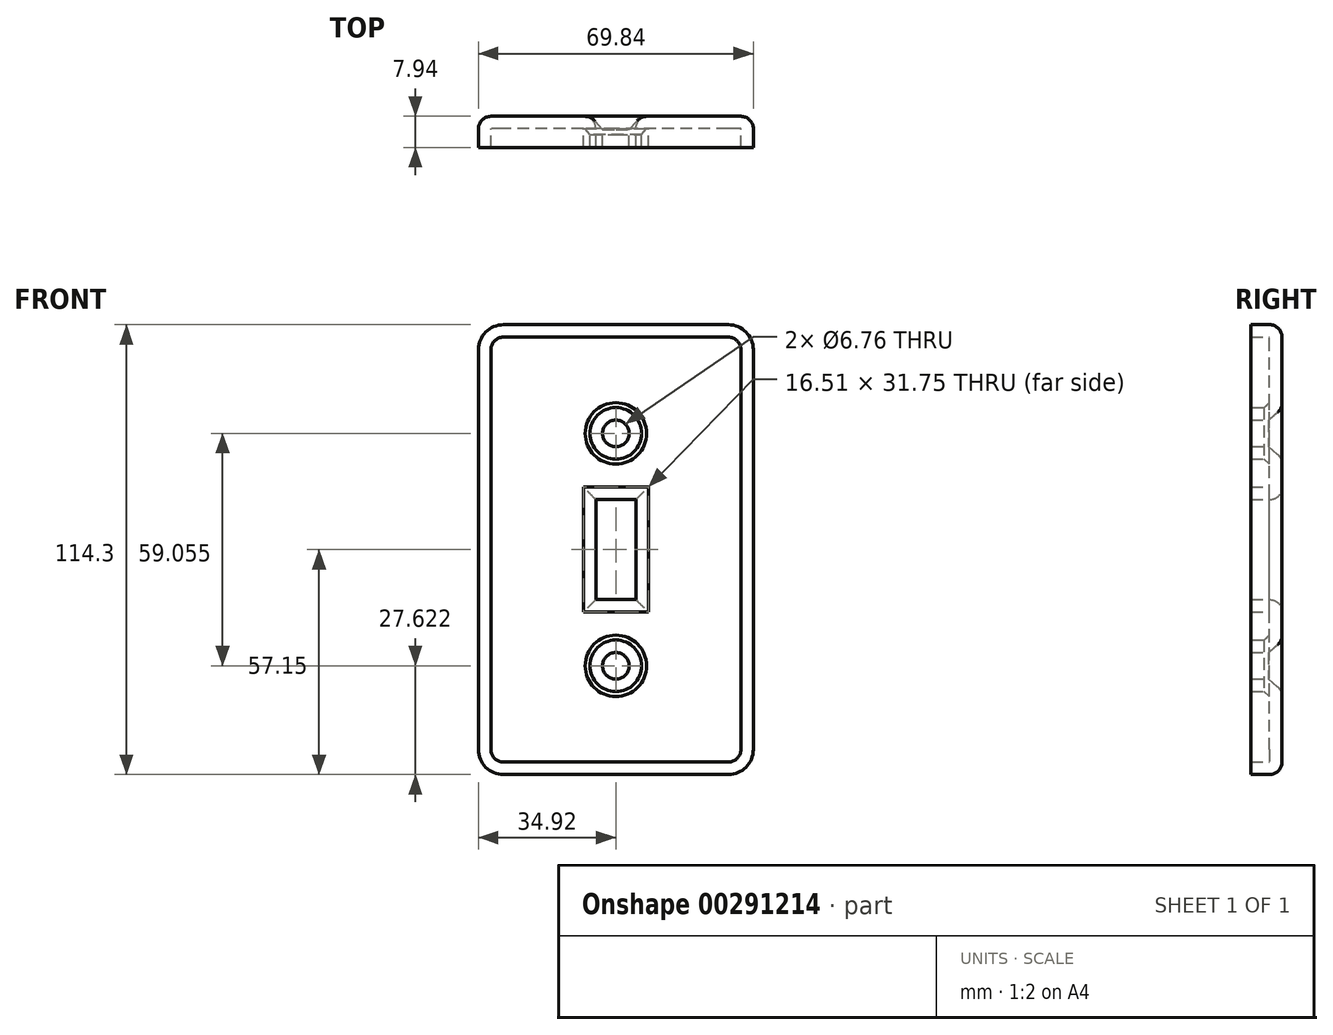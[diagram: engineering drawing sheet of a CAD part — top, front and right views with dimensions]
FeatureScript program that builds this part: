
annotation { "Feature Type Name" : "Feature", "Feature Type Description" : "" }
export const myFeature = defineFeature(function(context is Context, id is Id, definition is map)
    precondition{}
    {
        {
            var Q0;
            Q0=qCreatedBy(makeId("Front.planeOp"),FACE);
            var sketch = newSketch(context, id + "F0", { "sketchPlane" : qUnion([Q0])});
            skLineSegment(sketch, "E0.bottom", {"start": v(28.57, -57.15) * mm, "end": v(-28.57, -57.15) * mm});
            skLineSegment(sketch, "E0.top", {"start": v(28.58, 57.15) * mm, "end": v(-28.57, 57.15) * mm});
            skLineSegment(sketch, "E0.left", {"start": v(34.93, -50.8) * mm, "end": v(34.93, 50.8) * mm});
            skLineSegment(sketch, "E0.right", {"start": v(-34.92, -50.8) * mm, "end": v(-34.92, 50.8) * mm});
            skPoint(sketch, "E0.middle", {"position": v(0, 0) * mm});
            skPoint(sketch, "E1.visualSharp", {"position": v(-34.92, 57.15) * mm});
            skArc(sketch, "E1.filletArc", {"start": v(-28.57, 57.15) * mm, "mid": v(-33.07, 55.3) * mm, "end": v(-34.92, 50.8) * mm});
            skPoint(sketch, "E2.visualSharp", {"position": v(34.93, 57.15) * mm});
            skArc(sketch, "E2.filletArc", {"start": v(34.93, 50.8) * mm, "mid": v(33.07, 55.3) * mm, "end": v(28.58, 57.15) * mm});
            skPoint(sketch, "E3.visualSharp", {"position": v(34.92, -57.15) * mm});
            skArc(sketch, "E3.filletArc", {"start": v(28.57, -57.15) * mm, "mid": v(33.07, -55.3) * mm, "end": v(34.92, -50.8) * mm});
            skPoint(sketch, "E4.visualSharp", {"position": v(-34.93, -57.15) * mm});
            skArc(sketch, "E4.filletArc", {"start": v(-34.93, -50.8) * mm, "mid": v(-33.07, -55.3) * mm, "end": v(-28.57, -57.15) * mm});
            skLineSegment(sketch, "E5.bottom", {"start": v(5.08, -12.7) * mm, "end": v(-5.08, -12.7) * mm});
            skLineSegment(sketch, "E5.top", {"start": v(5.08, 12.7) * mm, "end": v(-5.08, 12.7) * mm});
            skLineSegment(sketch, "E5.left", {"start": v(5.08, -12.7) * mm, "end": v(5.08, 12.7) * mm});
            skLineSegment(sketch, "E5.right", {"start": v(-5.08, -12.7) * mm, "end": v(-5.08, 12.7) * mm});
            skPoint(sketch, "E6", {"position": v(0, 29.53) * mm});
            skPoint(sketch, "E7", {"position": v(0, -29.53) * mm});
            skSolve(sketch);
        }
        {
            var Q0;
            Q0=makeQuery(id+"F0.imprint","IMPRINT",FACE,{"disambiguationData":[TD([[makeQuery(id+"F0.imprint","IMPRINT",EDGE,{"derivedFrom":sQuery(id+"F0.wireOp",EDGE,"E0.bottom")}),-1.0]])]});
            extrude(context, id + "F1", {"entities" : qUnion([Q0]), "depth" : 7.94 * mm});
        }
        {
            var Q0;
            Q0=sQuery(id+"F0.wireOp",VERTEX,"E7");
            var Q1;
            Q1=sQuery(id+"F0.wireOp",VERTEX,"E6");
            var Q2;
            Q2=makeQuery(id+"F1.opExtrude","SWEPT_BODY",BODY,{"disambiguationData":[OSD([sQuery(id+"F0.wireOp",EDGE,"E0.bottom"),sQuery(id+"F0.wireOp",EDGE,"E0.top"),sQuery(id+"F0.wireOp",EDGE,"E0.left"),sQuery(id+"F0.wireOp",EDGE,"E0.right"),sQuery(id+"F0.wireOp",EDGE,"E1.filletArc"),sQuery(id+"F0.wireOp",EDGE,"E2.filletArc"),sQuery(id+"F0.wireOp",EDGE,"E3.filletArc"),sQuery(id+"F0.wireOp",EDGE,"E4.filletArc"),sQuery(id+"F0.wireOp",EDGE,"E5.bottom"),sQuery(id+"F0.wireOp",EDGE,"E5.top"),sQuery(id+"F0.wireOp",EDGE,"E5.left"),sQuery(id+"F0.wireOp",EDGE,"E5.right")])]});
            hole(context, id + "F2", {"style" : HoleStyle.C_SINK, "endStyle" : HoleEndStyle.THROUGH, "oppositeDirection" : true, "holeDiameter" : 6.76 * mm, "cSinkDiameter" : 12.7 * mm, "cSinkAngle" : 82 * degree, "tappedDepth" : 12.7 * mm, "tapClearance" : 3, "locations" : qUnion([Q0, Q1]), "scope" : qUnion([Q2])});
        }
        {
            var Q0;
            Q0=makeQuery(id+"F1.opExtrude","CAP_FACE",FACE,{"disambiguationData":[OSD([sQuery(id+"F0.wireOp",EDGE,"E0.bottom"),sQuery(id+"F0.wireOp",EDGE,"E0.top"),sQuery(id+"F0.wireOp",EDGE,"E0.left"),sQuery(id+"F0.wireOp",EDGE,"E0.right"),sQuery(id+"F0.wireOp",EDGE,"E1.filletArc"),sQuery(id+"F0.wireOp",EDGE,"E2.filletArc"),sQuery(id+"F0.wireOp",EDGE,"E3.filletArc"),sQuery(id+"F0.wireOp",EDGE,"E4.filletArc"),sQuery(id+"F0.wireOp",EDGE,"E5.bottom"),sQuery(id+"F0.wireOp",EDGE,"E5.top"),sQuery(id+"F0.wireOp",EDGE,"E5.left"),sQuery(id+"F0.wireOp",EDGE,"E5.right")])],"isStart":true});
            fillet(context, id + "F3", {"entities" : qUnion([Q0]), "radius" : 3.17 * mm, "tangentPropagation" : true, "allowEdgeOverflow" : false});
        }
        {
            var Q0;
            Q0=makeQuery(id+"F1.opExtrude","CAP_FACE",FACE,{"disambiguationData":[OSD([sQuery(id+"F0.wireOp",EDGE,"E0.bottom"),sQuery(id+"F0.wireOp",EDGE,"E0.top"),sQuery(id+"F0.wireOp",EDGE,"E0.left"),sQuery(id+"F0.wireOp",EDGE,"E0.right"),sQuery(id+"F0.wireOp",EDGE,"E1.filletArc"),sQuery(id+"F0.wireOp",EDGE,"E2.filletArc"),sQuery(id+"F0.wireOp",EDGE,"E3.filletArc"),sQuery(id+"F0.wireOp",EDGE,"E4.filletArc"),sQuery(id+"F0.wireOp",EDGE,"E5.bottom"),sQuery(id+"F0.wireOp",EDGE,"E5.top"),sQuery(id+"F0.wireOp",EDGE,"E5.left"),sQuery(id+"F0.wireOp",EDGE,"E5.right")])],"isStart":false});
            shell(context, id + "F4", {"entities" : qUnion([Q0]), "thickness" : 3.17 * mm});
        }
    });
